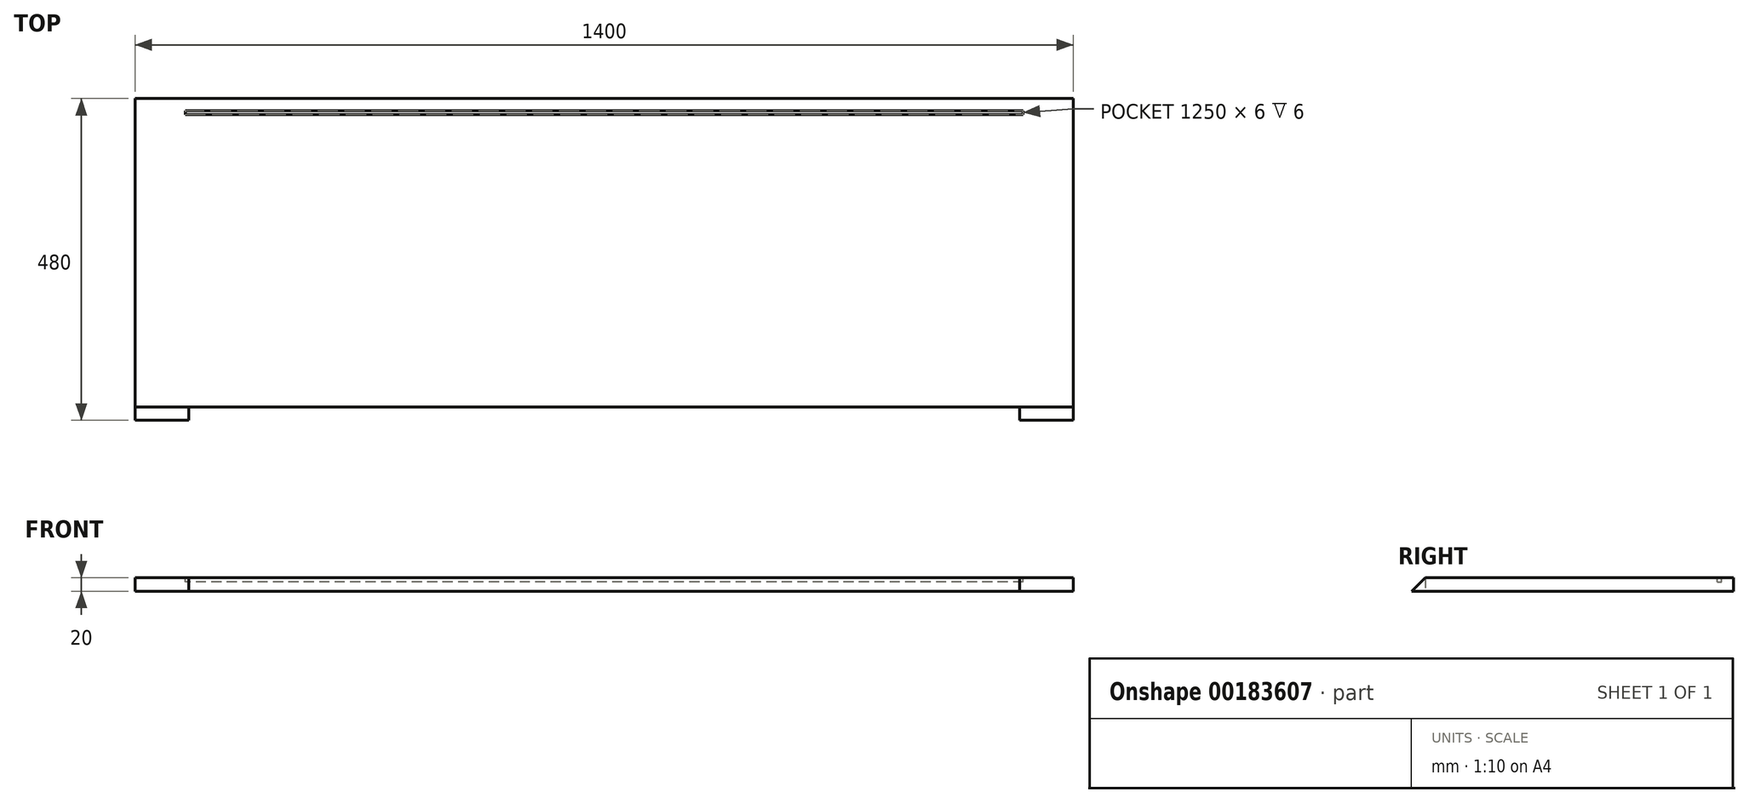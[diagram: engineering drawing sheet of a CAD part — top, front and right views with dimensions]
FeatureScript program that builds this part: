
annotation { "Feature Type Name" : "Feature", "Feature Type Description" : "" }
export const myFeature = defineFeature(function(context is Context, id is Id, definition is map)
    precondition{}
    {
        {
            var Q0;
            Q0=qCreatedBy(makeId("Top.planeOp"),FACE);
            var sketch = newSketch(context, id + "F0", { "sketchPlane" : qUnion([Q0])});
            skLineSegment(sketch, "E0.bottom", {"start": v(700, -240) * mm, "end": v(-700, -240) * mm});
            skLineSegment(sketch, "E0.top", {"start": v(700, 240) * mm, "end": v(-700, 240) * mm});
            skLineSegment(sketch, "E0.left", {"start": v(700, -240) * mm, "end": v(700, 240) * mm});
            skLineSegment(sketch, "E0.right", {"start": v(-700, -240) * mm, "end": v(-700, 240) * mm});
            skPoint(sketch, "E0.middle", {"position": v(0, 0) * mm});
            skSolve(sketch);
        }
        {
            var Q0;
            Q0 = qSketchRegion(id + "F0", true);
            extrude(context, id + "F1", {"entities" : qUnion([Q0]), "depth" : 20 * mm});
        }
        {
            var Q0;
            Q0=makeQuery(id+"F1.opExtrude","SWEPT_FACE",FACE,{"disambiguationData":[OSD([sQuery(id+"F0.wireOp",EDGE,"E0.left")])]});
            var sketch = newSketch(context, id + "F2", { "sketchPlane" : qUnion([Q0])});
            skLineSegment(sketch, "E1", {"start": v(-240, 0) * mm, "end": v(-220, 20) * mm});
            skLineSegment(sketch, "E2", {"start": v(-220, 20) * mm, "end": v(-240, 20) * mm});
            skLineSegment(sketch, "E3", {"start": v(-240, 20) * mm, "end": v(-240, 0) * mm});
            skSolve(sketch);
        }
        {
            var Q0;
            Q0 = qSketchRegion(id + "F2", true);
            extrude(context, id + "F3", {"entities" : qUnion([Q0]), "operationType" : NewBodyOperationType.REMOVE, "oppositeDirection" : true, "depth" : 1400 * mm});
        }
        {
            var Q0;
            Q0=makeQuery(id+"F1.opExtrude","CAP_FACE",FACE,{"disambiguationData":[OSD([sQuery(id+"F0.wireOp",EDGE,"E0.bottom"),sQuery(id+"F0.wireOp",EDGE,"E0.top"),sQuery(id+"F0.wireOp",EDGE,"E0.left"),sQuery(id+"F0.wireOp",EDGE,"E0.right")])],"isStart":false});
            var sketch = newSketch(context, id + "F4", { "sketchPlane" : qUnion([Q0])});
            skLineSegment(sketch, "E4.bottom", {"start": v(625, 216) * mm, "end": v(-625, 216) * mm});
            skLineSegment(sketch, "E4.top", {"start": v(625, 222) * mm, "end": v(-625, 222) * mm});
            skLineSegment(sketch, "E4.left", {"start": v(625, 216) * mm, "end": v(625, 222) * mm});
            skLineSegment(sketch, "E4.right", {"start": v(-625, 216) * mm, "end": v(-625, 222) * mm});
            skSolve(sketch);
        }
        {
            var Q0;
            Q0 = qSketchRegion(id + "F4", true);
            extrude(context, id + "F5", {"entities" : qUnion([Q0]), "operationType" : NewBodyOperationType.REMOVE, "oppositeDirection" : true, "depth" : 6 * mm});
        }
        {
            var Q0;
            Q0=makeQuery(id+"F1.opExtrude","CAP_FACE",FACE,{"disambiguationData":[OSD([sQuery(id+"F0.wireOp",EDGE,"E0.bottom"),sQuery(id+"F0.wireOp",EDGE,"E0.top"),sQuery(id+"F0.wireOp",EDGE,"E0.left"),sQuery(id+"F0.wireOp",EDGE,"E0.right")])],"isStart":true});
            var sketch = newSketch(context, id + "F6", { "sketchPlane" : qUnion([Q0])});
            skLineSegment(sketch, "E5.bottom", {"start": v(-620, 240) * mm, "end": v(620, 240) * mm});
            skLineSegment(sketch, "E5.top", {"start": v(-620, 220) * mm, "end": v(620, 220) * mm});
            skLineSegment(sketch, "E5.left", {"start": v(-620, 240) * mm, "end": v(-620, 220) * mm});
            skLineSegment(sketch, "E5.right", {"start": v(620, 240) * mm, "end": v(620, 220) * mm});
            skSolve(sketch);
        }
        {
            var Q0;
            Q0 = qSketchRegion(id + "F6", true);
            extrude(context, id + "F7", {"entities" : qUnion([Q0]), "operationType" : NewBodyOperationType.REMOVE, "oppositeDirection" : true, "depth" : 20 * mm});
        }
    });
